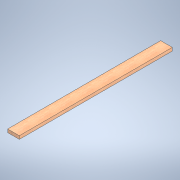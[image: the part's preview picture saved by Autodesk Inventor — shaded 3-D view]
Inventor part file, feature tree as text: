
AUTODESK INVENTOR PART (.ipt)
format: ipt  version: 2020.2 (Build 242310000, 310)  size: 100,352 bytes
history: native  units: in
note: dims shown in document units (in); Inventor stores cm internally (conversion verified against a paired STEP export)
features: extrude x1, sketch x1
ambient origin geometry x8: Origin, YZ Plane, XZ Plane, XY Plane, X Axis, Y Axis, Z Axis, Center Point
bodies: Solid1 (feature_tree)
feature tree (2):
  extrude  "Extrusion1"  Depth=1.5in
  sketch  "Sketch1"  dims[d0=5.5in d1=1.5in d2=72.0in d3=0.0in]
